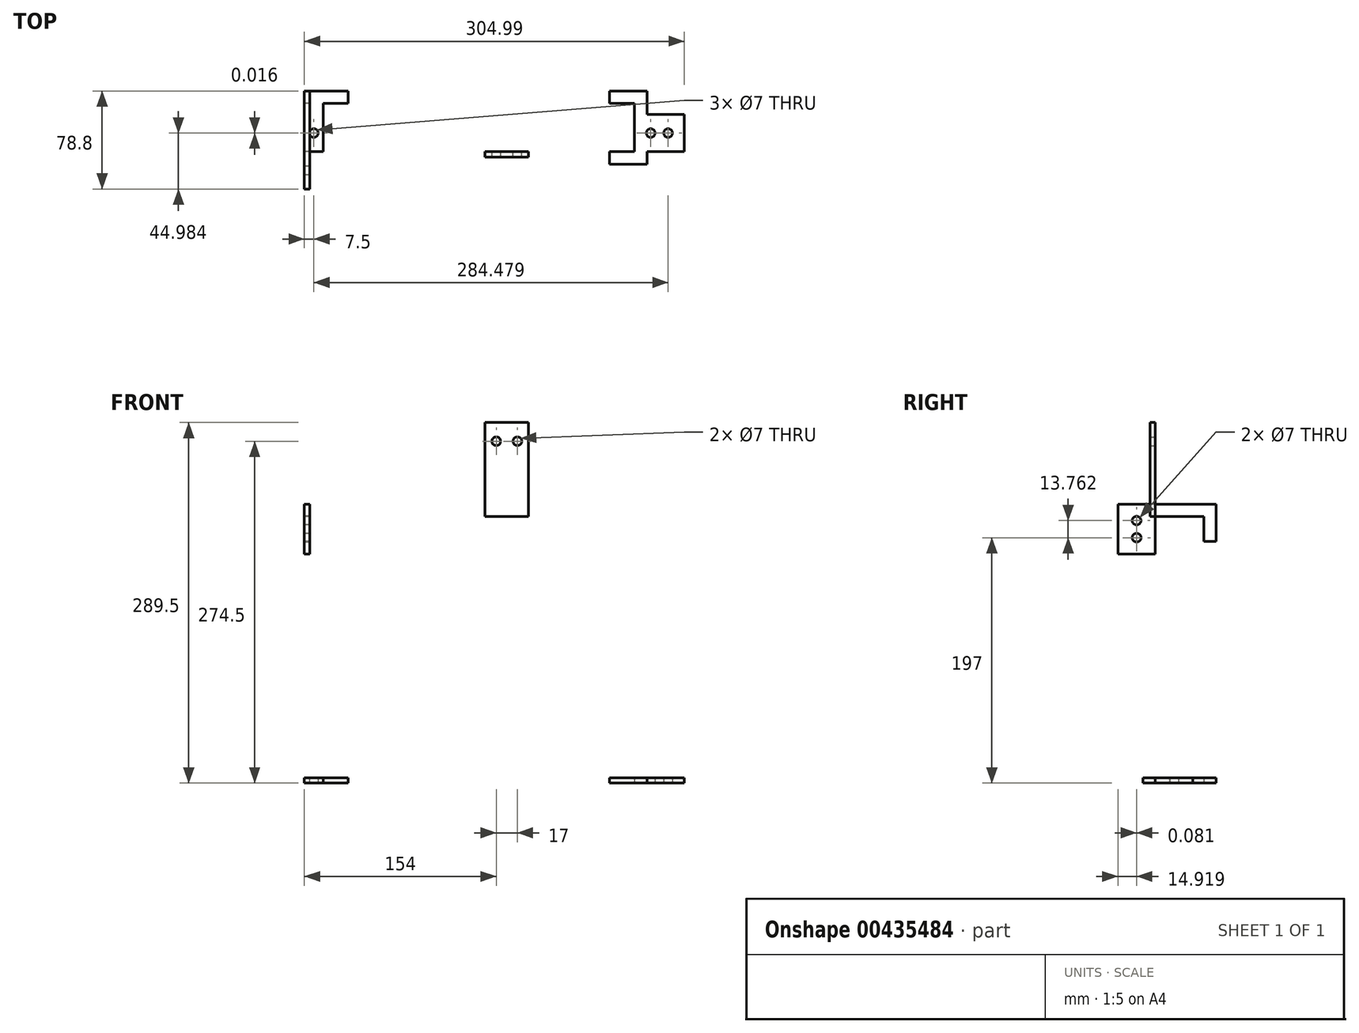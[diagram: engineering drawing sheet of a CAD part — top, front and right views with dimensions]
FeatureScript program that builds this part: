
annotation { "Feature Type Name" : "Feature", "Feature Type Description" : "" }
export const myFeature = defineFeature(function(context is Context, id is Id, definition is map)
    precondition{}
    {
        {
            var Q0;
            Q0=qCreatedBy(makeId("Top.planeOp"),FACE);
            var sketch = newSketch(context, id + "F0", { "sketchPlane" : qUnion([Q0])});
            skLineSegment(sketch, "E0", {"start": v(35, 38.8) * mm, "end": v(15, 38.8) * mm});
            skLineSegment(sketch, "E1", {"start": v(15, 38.8) * mm, "end": v(15, 0) * mm});
            skLineSegment(sketch, "E2", {"start": v(15, 0) * mm, "end": v(0, 0) * mm});
            skLineSegment(sketch, "E3", {"start": v(35, 38.8) * mm, "end": v(35, 48.8) * mm});
            skLineSegment(sketch, "E4", {"start": v(35, 48.8) * mm, "end": v(0, 48.8) * mm});
            skLineSegment(sketch, "E5", {"start": v(0, 48.8) * mm, "end": v(0, 0) * mm});
            skLineSegment(sketch, "E6", {"start": v(7.5, 0) * mm, "end": v(7.5, 15) * mm, "construction": true});
            skCircle(sketch, "E7", {"center": v(7.5, 15) * mm, "radius": 3.5 * mm});
            skLineSegment(sketch, "E8", {"start": v(264.99, 0) * mm, "end": v(264.99, 38.8) * mm});
            skLineSegment(sketch, "E9", {"start": v(264.99, 0) * mm, "end": v(244.99, 0) * mm});
            skLineSegment(sketch, "E10", {"start": v(244.99, 0) * mm, "end": v(244.99, -10) * mm});
            skLineSegment(sketch, "E11", {"start": v(0, 0) * mm, "end": v(244.99, 0) * mm, "construction": true});
            skLineSegment(sketch, "E12", {"start": v(264.99, 38.8) * mm, "end": v(244.99, 38.8) * mm});
            skLineSegment(sketch, "E13", {"start": v(244.99, 38.8) * mm, "end": v(244.99, 48.8) * mm});
            skLineSegment(sketch, "E14", {"start": v(244.99, 48.8) * mm, "end": v(274.99, 48.8) * mm});
            skLineSegment(sketch, "E15", {"start": v(304.99, 29.98) * mm, "end": v(274.99, 30) * mm});
            skLineSegment(sketch, "E16", {"start": v(274.99, 30) * mm, "end": v(274.99, 48.8) * mm});
            skLineSegment(sketch, "E17", {"start": v(274.99, -10) * mm, "end": v(274.97, 0) * mm});
            skLineSegment(sketch, "E18", {"start": v(274.97, 0) * mm, "end": v(304.97, -0.02) * mm});
            skLineSegment(sketch, "E19", {"start": v(304.99, 29.98) * mm, "end": v(304.97, -0.02) * mm});
            skLineSegment(sketch, "E20", {"start": v(244.99, -10) * mm, "end": v(274.99, -10) * mm});
            skLineSegment(sketch, "E21", {"start": v(291.98, 14.98) * mm, "end": v(304.98, 14.98) * mm, "construction": true});
            skPoint(sketch, "E21.startSnap0", {"position": v(304.98, 14.98) * mm});
            skLineSegment(sketch, "E22", {"start": v(264.99, 14.98) * mm, "end": v(277.99, 14.98) * mm, "construction": true});
            skCircle(sketch, "E23", {"center": v(277.99, 14.98) * mm, "radius": 3.5 * mm});
            skCircle(sketch, "E24", {"center": v(291.98, 14.98) * mm, "radius": 3.5 * mm});
            skSolve(sketch);
        }
        {
            var Q0;
            Q0=makeQuery(id+"F0.imprint","IMPRINT",FACE,{"disambiguationData":[TD([[makeQuery(id+"F0.imprint","IMPRINT",EDGE,{"derivedFrom":sQuery(id+"F0.wireOp",EDGE,"E0")}),-1.0]])]});
            var Q1;
            Q1=makeQuery(id+"F0.imprint","IMPRINT",FACE,{"disambiguationData":[TD([[makeQuery(id+"F0.imprint","IMPRINT",EDGE,{"derivedFrom":sQuery(id+"F0.wireOp",EDGE,"E8")}),-1.0]])]});
            extrude(context, id + "F1", {"entities" : qUnion([Q0, Q1]), "depth" : 4.3 * mm});
        }
        {
            var Q0;
            Q0=qCreatedBy(makeId("Right.planeOp"),FACE);
            var sketch = newSketch(context, id + "F2", { "sketchPlane" : qUnion([Q0])});
            skLineSegment(sketch, "E25", {"start": v(0, 0) * mm, "end": v(0, 214) * mm});
            skLineSegment(sketch, "E26", {"start": v(0, 214) * mm, "end": v(38.8, 214) * mm});
            skLineSegment(sketch, "E27", {"start": v(38.8, 214) * mm, "end": v(38.8, 194) * mm});
            skLineSegment(sketch, "E28", {"start": v(38.8, 194) * mm, "end": v(48.8, 194) * mm});
            skLineSegment(sketch, "E29", {"start": v(48.8, 194) * mm, "end": v(48.8, 224) * mm});
            skLineSegment(sketch, "E30", {"start": v(48.8, 224) * mm, "end": v(-30, 224) * mm});
            skLineSegment(sketch, "E31", {"start": v(-30, 224) * mm, "end": v(-30, 184) * mm});
            skLineSegment(sketch, "E32", {"start": v(-30, 184) * mm, "end": v(0, 184) * mm});
            skLineSegment(sketch, "E33", {"start": v(0, 184) * mm, "end": v(0, 214) * mm});
            skLineSegment(sketch, "E34", {"start": v(-15, 184) * mm, "end": v(-15, 197) * mm, "construction": true});
            skLineSegment(sketch, "E35", {"start": v(-15, 224) * mm, "end": v(-15, 211) * mm, "construction": true});
            skCircle(sketch, "E36", {"center": v(-15.08, 210.76) * mm, "radius": 3.5 * mm});
            skCircle(sketch, "E37", {"center": v(-15, 197) * mm, "radius": 3.5 * mm});
            skSolve(sketch);
        }
        {
            var Q0;
            Q0 = qSketchRegion(id + "F2", true);
            extrude(context, id + "F3", {"entities" : qUnion([Q0]), "depth" : 4.3 * mm});
        }
        {
            var Q0;
            Q0=qCreatedBy(makeId("Front.planeOp"),FACE);
            var sketch = newSketch(context, id + "F4", { "sketchPlane" : qUnion([Q0])});
            skLineSegment(sketch, "E38", {"start": v(0, 0) * mm, "end": v(180, 0) * mm});
            skLineSegment(sketch, "E39", {"start": v(180, 0) * mm, "end": v(180, 214) * mm});
            skLineSegment(sketch, "E40", {"start": v(180, 214) * mm, "end": v(145, 214) * mm});
            skLineSegment(sketch, "E41", {"start": v(145, 214) * mm, "end": v(145, 289.5) * mm});
            skLineSegment(sketch, "E42", {"start": v(145, 289.5) * mm, "end": v(180, 289.5) * mm});
            skLineSegment(sketch, "E43", {"start": v(180, 289.5) * mm, "end": v(180, 214) * mm});
            skLineSegment(sketch, "E44", {"start": v(162.5, 289.5) * mm, "end": v(162.5, 274.5) * mm, "construction": true});
            skLineSegment(sketch, "E45", {"start": v(145, 274.5) * mm, "end": v(154, 274.5) * mm, "construction": true});
            skLineSegment(sketch, "E46", {"start": v(180, 274.5) * mm, "end": v(171, 274.5) * mm, "construction": true});
            skCircle(sketch, "E47", {"center": v(154, 274.5) * mm, "radius": 3.5 * mm});
            skCircle(sketch, "E48", {"center": v(171, 274.5) * mm, "radius": 3.5 * mm});
            skSolve(sketch);
        }
        {
            var Q0;
            Q0=makeQuery(id+"F4.imprint","IMPRINT",FACE,{"disambiguationData":[TD([[makeQuery(id+"F4.imprint","IMPRINT",EDGE,{"derivedFrom":sQuery(id+"F4.wireOp",EDGE,"E40")}),-1.0]])]});
            extrude(context, id + "F5", {"entities" : qUnion([Q0]), "depth" : 4.3 * mm});
        }
    });
